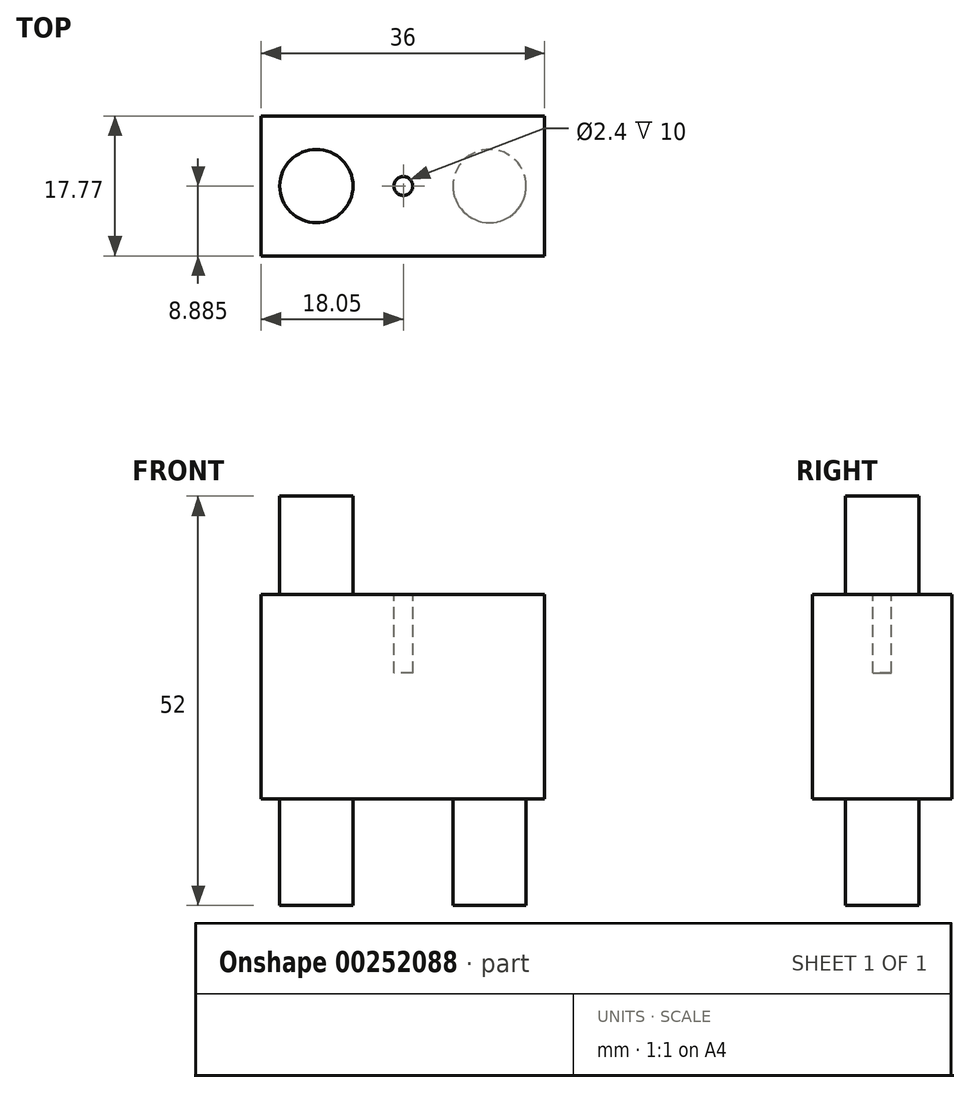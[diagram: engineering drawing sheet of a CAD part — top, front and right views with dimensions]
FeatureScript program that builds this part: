
annotation { "Feature Type Name" : "Feature", "Feature Type Description" : "" }
export const myFeature = defineFeature(function(context is Context, id is Id, definition is map)
    precondition{}
    {
        {
            var Q0;
            Q0=qCreatedBy(makeId("Front.planeOp"),FACE);
            var sketch = newSketch(context, id + "F0", { "sketchPlane" : qUnion([Q0])});
            skLineSegment(sketch, "E0.bottom", {"start": v(0, 0) * mm, "end": v(36, 0) * mm});
            skLineSegment(sketch, "E0.top", {"start": v(0, 26) * mm, "end": v(36, 26) * mm});
            skLineSegment(sketch, "E0.left", {"start": v(0, 0) * mm, "end": v(0, 26) * mm});
            skLineSegment(sketch, "E0.right", {"start": v(36, 0) * mm, "end": v(36, 26) * mm});
            skSolve(sketch);
        }
        {
            var Q0;
            Q0=makeQuery(id+"F0.imprint","IMPRINT",FACE,{"disambiguationData":[TD([[makeQuery(id+"F0.imprint","IMPRINT",EDGE,{"derivedFrom":sQuery(id+"F0.wireOp",EDGE,"E0.bottom")}),1.0]])]});
            extrude(context, id + "F1", {"entities" : qUnion([Q0]), "depth" : 17.77 * mm});
        }
        {
            var Q0;
            Q0=makeQuery(id+"F1.opExtrude","SWEPT_FACE",FACE,{"disambiguationData":[OSD([sQuery(id+"F0.wireOp",EDGE,"E0.top")])]});
            var sketch = newSketch(context, id + "F2", { "sketchPlane" : qUnion([Q0])});
            skCircle(sketch, "E1", {"center": v(7, -8.88) * mm, "radius": 4.65 * mm});
            skPoint(sketch, "E1.centerSnap0", {"position": v(0, -8.88) * mm});
            skCircle(sketch, "E2", {"center": v(18.05, -8.88) * mm, "radius": 1.2 * mm});
            skSolve(sketch);
        }
        {
            var Q0;
            Q0=makeQuery(id+"F2.imprint","IMPRINT",FACE,{"disambiguationData":[TD([[makeQuery(id+"F2.imprint","IMPRINT",EDGE,{"derivedFrom":sQuery(id+"F2.wireOp",EDGE,"E1")}),1.0]])]});
            extrude(context, id + "F3", {"entities" : qUnion([Q0]), "operationType" : NewBodyOperationType.ADD, "depth" : 12.5 * mm});
        }
        {
            var Q0;
            Q0=makeQuery(id+"F2.imprint","IMPRINT",FACE,{"disambiguationData":[TD([[makeQuery(id+"F2.imprint","IMPRINT",EDGE,{"derivedFrom":sQuery(id+"F2.wireOp",EDGE,"E2")}),1.0]])]});
            extrude(context, id + "F4", {"entities" : qUnion([Q0]), "operationType" : NewBodyOperationType.REMOVE, "oppositeDirection" : true, "depth" : 10 * mm});
        }
        {
            var Q0;
            Q0=makeQuery(id+"F1.opExtrude","SWEPT_FACE",FACE,{"disambiguationData":[OSD([sQuery(id+"F0.wireOp",EDGE,"E0.bottom")])]});
            var sketch = newSketch(context, id + "F5", { "sketchPlane" : qUnion([Q0])});
            skCircle(sketch, "E3", {"center": v(7, 8.88) * mm, "radius": 4.65 * mm});
            skPoint(sketch, "E3.centerSnap0", {"position": v(0, 8.88) * mm});
            skCircle(sketch, "E4", {"center": v(29, 8.88) * mm, "radius": 4.65 * mm});
            skPoint(sketch, "E4.centerSnap0", {"position": v(36, 8.88) * mm});
            skSolve(sketch);
        }
        {
            var Q0;
            Q0=makeQuery(id+"F5.imprint","IMPRINT",FACE,{"disambiguationData":[TD([[makeQuery(id+"F5.imprint","IMPRINT",EDGE,{"derivedFrom":sQuery(id+"F5.wireOp",EDGE,"E3")}),1.0]])]});
            var Q1;
            Q1=makeQuery(id+"F5.imprint","IMPRINT",FACE,{"disambiguationData":[TD([[makeQuery(id+"F5.imprint","IMPRINT",EDGE,{"derivedFrom":sQuery(id+"F5.wireOp",EDGE,"E4")}),1.0]])]});
            extrude(context, id + "F6", {"entities" : qUnion([Q0, Q1]), "operationType" : NewBodyOperationType.ADD, "depth" : 13.5 * mm});
        }
    });
